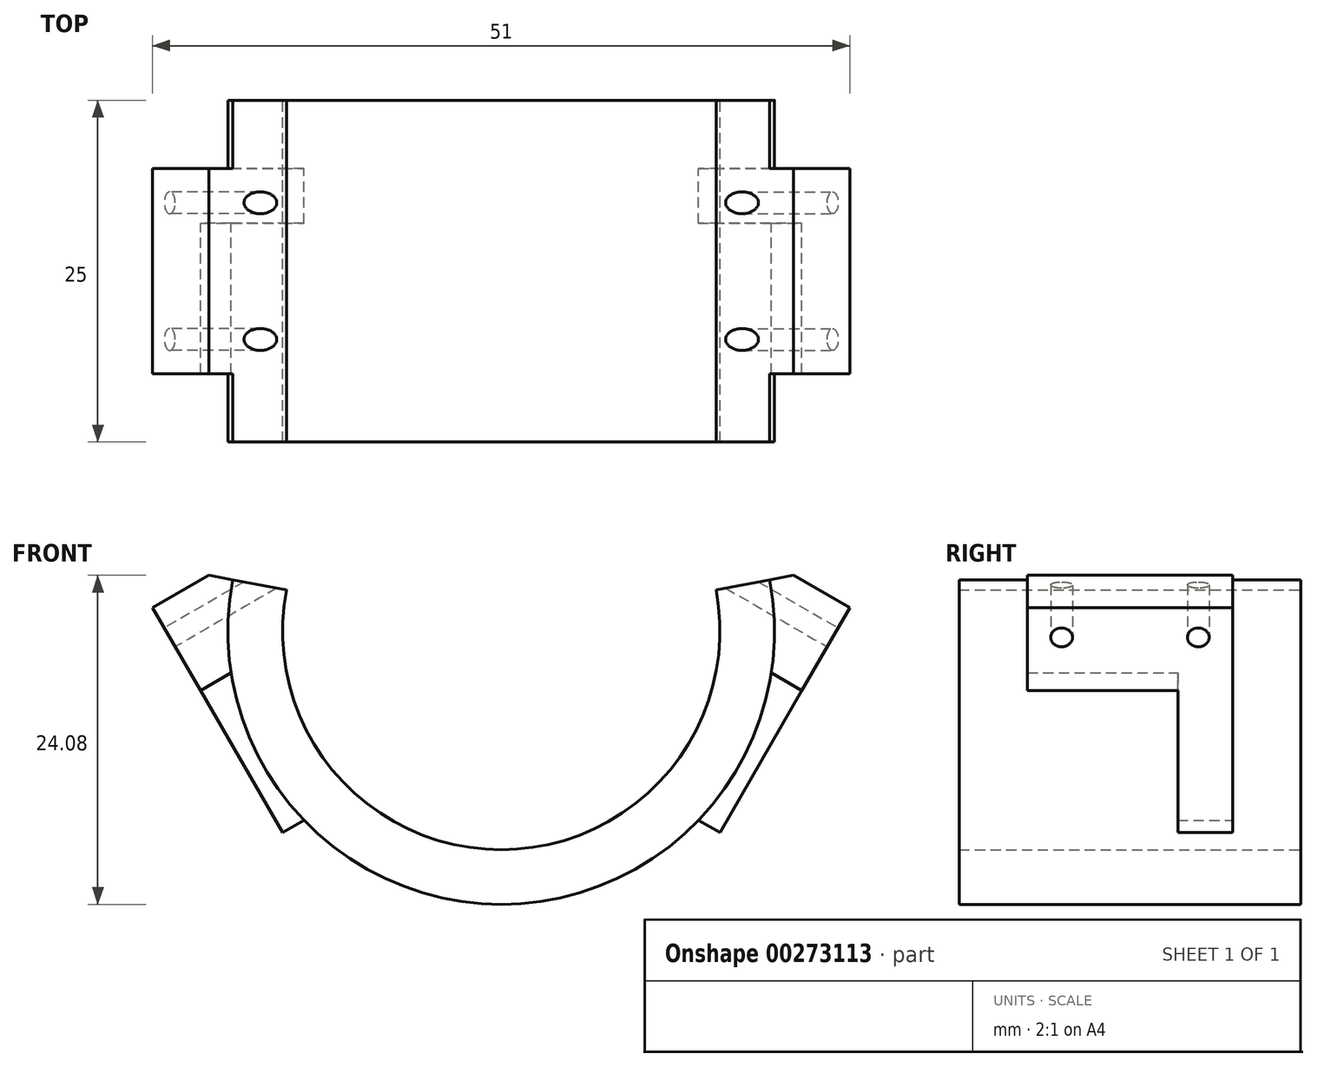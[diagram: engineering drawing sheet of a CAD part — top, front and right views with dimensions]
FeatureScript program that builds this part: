
annotation { "Feature Type Name" : "Feature", "Feature Type Description" : "" }
export const myFeature = defineFeature(function(context is Context, id is Id, definition is map)
    precondition{}
    {
        {
            var Q0;
            Q0=qCreatedBy(makeId("Front.planeOp"),FACE);
            var sketch = newSketch(context, id + "F0", { "sketchPlane" : qUnion([Q0])});
            skArc(sketch, "E0", {"start": v(0, -16) * mm, "mid": v(12.33, -10.2) * mm, "end": v(15.72, 3) * mm});
            skLineSegment(sketch, "E1", {"start": v(25.5, 1.7) * mm, "end": v(16, -14.75) * mm});
            skLineSegment(sketch, "E2", {"start": v(25.5, 1.7) * mm, "end": v(21.38, 4.08) * mm});
            skLineSegment(sketch, "E3", {"start": v(15.72, 3) * mm, "end": v(21.38, 4.08) * mm});
            skLineSegment(sketch, "E4", {"start": v(16, -14.75) * mm, "end": v(14.43, -13.85) * mm});
            skLineSegment(sketch, "E5", {"start": v(22, -4.36) * mm, "end": v(19.76, -3.07) * mm});
            skLineSegment(sketch, "E6", {"start": v(0, -16) * mm, "end": v(0, -20) * mm});
            skArc(sketch, "E7.trimOffspring", {"start": v(0, -20) * mm, "mid": v(15.41, -12.75) * mm, "end": v(19.65, 3.75) * mm});
            skPoint(sketch, "E8.orphan", {"position": v(-16, -14.75) * mm});
            skPoint(sketch, "E9.orphan", {"position": v(-14.43, -13.85) * mm});
            skPoint(sketch, "E10.MirrorCS.start.orphan", {"position": v(-22, -4.36) * mm});
            skPoint(sketch, "E11.end.orphan", {"position": v(-19.76, -3.07) * mm});
            skPoint(sketch, "E12.MirrorCS.start.orphan", {"position": v(-15.72, 3) * mm});
            skPoint(sketch, "E13.MirrorCS.end.orphan", {"position": v(-21.38, 4.08) * mm});
            skPoint(sketch, "E13.MirrorCS.start.orphan", {"position": v(-25.5, 1.7) * mm});
            skSolve(sketch);
        }
        {
            var Q0;
            {var subQ5=sQuery(id+"F0.wireOp",EDGE,"E0");Q0=makeQuery(id+"F0.imprint","IMPRINT",FACE,{"disambiguationData":[TD([[makeQuery(id+"F0.imprint","IMPRINT",EDGE,{"derivedFrom":subQ5}),-1.0]])]});}
            extrude(context, id + "F1", {"entities" : qUnion([Q0]), "depth" : 20 * mm});
        }
        {
            var Q0;
            Q0=makeQuery(id+"F1.opExtrude","CAP_FACE",FACE,{"disambiguationData":[OSD([sQuery(id+"F0.wireOp",EDGE,"E0"),sQuery(id+"F0.wireOp",EDGE,"E11"),sQuery(id+"F0.wireOp",EDGE,"E3"),sQuery(id+"F0.wireOp",EDGE,"E12.MirrorCS")])],"isStart":true});
            var Q1;
            Q1 = qConstructionFilter(qBodyType(qCreatedBy(id + "F0" ,EDGE), BodyType.WIRE), ConstructionObject.NO);
            extrude(context, id + "F2", {"entities" : qUnion([Q0]), "operationType" : NewBodyOperationType.ADD, "surfaceEntities" : qUnion([Q1]), "depth" : 5 * mm});
        }
        {
            var Q0;
            Q0 = qSketchRegion(id + "F0", true);
            extrude(context, id + "F3", {"entities" : qUnion([Q0]), "operationType" : NewBodyOperationType.ADD, "depth" : 4 * mm});
        }
        {
            var Q0;
            {var subQ3=sQuery(id+"F0.wireOp",EDGE,"E2");Q0=makeQuery(id+"F0.imprint","IMPRINT",FACE,{"disambiguationData":[TD([[makeQuery(id+"F0.imprint","IMPRINT",EDGE,{"derivedFrom":subQ3}),1.0]])]});}
            var Q1;
            {var subQ1=sQuery(id+"F0.wireOp",EDGE,"E10.MirrorCS");Q1=makeQuery(id+"F0.imprint","IMPRINT",FACE,{"disambiguationData":[TD([[makeQuery(id+"F0.imprint","IMPRINT",EDGE,{"derivedFrom":subQ1}),1.0]])]});}
            var Q2;
            Q2=sQuery(id+"F0.wireOp",EDGE,"E2");
            extrude(context, id + "F4", {"entities" : qUnion([Q0, Q1]), "operationType" : NewBodyOperationType.ADD, "surfaceEntities" : qUnion([Q2]), "depth" : 15 * mm});
        }
        {
            var Q0;
            {var subQ0=sQuery(id+"F0.wireOp",EDGE,"E1");Q0=makeQuery(id+"F4.boolean.opBoolean","MERGE",FACE,{"derivedFrom":[makeQuery(id+"F3.opExtrude","SWEPT_FACE",FACE,{"disambiguationData":[OSD([subQ0])]}),makeQuery(id+"F4.opExtrude","SWEPT_FACE",FACE,{"disambiguationData":[OSD([subQ0])]})]});}
            var sketch = newSketch(context, id + "F5", { "sketchPlane" : qUnion([Q0])});
            skLineSegment(sketch, "E14", {"start": v(32.62, -7.81) * mm, "end": v(8.42, -7.81) * mm, "construction": true});
            skLineSegment(sketch, "E15", {"start": v(-7.5, 16.75) * mm, "end": v(-7.5, 2.83) * mm, "construction": true});
            skLineSegment(sketch, "E16", {"start": v(-16.9, 11.72) * mm, "end": v(2.1, 11.72) * mm, "construction": true});
            skCircle(sketch, "E17", {"center": v(-12.5, 11.72) * mm, "radius": 0.8 * mm});
            skCircle(sketch, "E18", {"center": v(-2.5, 11.72) * mm, "radius": 0.8 * mm});
            skSolve(sketch);
        }
        {
            var Q0;
            Q0 = qSketchRegion(id + "F5", true);
            var Q1;
            Q1=sQuery(id+"F5.wireOp",EDGE,"E17");
            var Q2;
            Q2=sQuery(id+"F5.wireOp",EDGE,"E18");
            extrude(context, id + "F6", {"entities" : qUnion([Q0]), "operationType" : NewBodyOperationType.REMOVE, "surfaceEntities" : qUnion([Q1, Q2]), "endBound" : BoundingType.UP_TO_NEXT, "oppositeDirection" : true, "depth" : 5 * mm});
        }
        {
            var Q0;
            Q0=makeQuery(id+"F1.opExtrude","SWEPT_BODY",BODY,{"disambiguationData":[OSD([sQuery(id+"F0.wireOp",EDGE,"E0"),sQuery(id+"F0.wireOp",EDGE,"E3"),sQuery(id+"F0.wireOp",EDGE,"E6"),sQuery(id+"F0.wireOp",EDGE,"E7.trimOffspring")])]});
            var Q1;
            Q1=qCreatedBy(makeId("Right.planeOp"),FACE);
            mirror(context, id + "F7", {"operationType" : NewBodyOperationType.ADD, "entities" : qUnion([Q0]), "mirrorPlane" : qUnion([Q1])});
        }
    });
